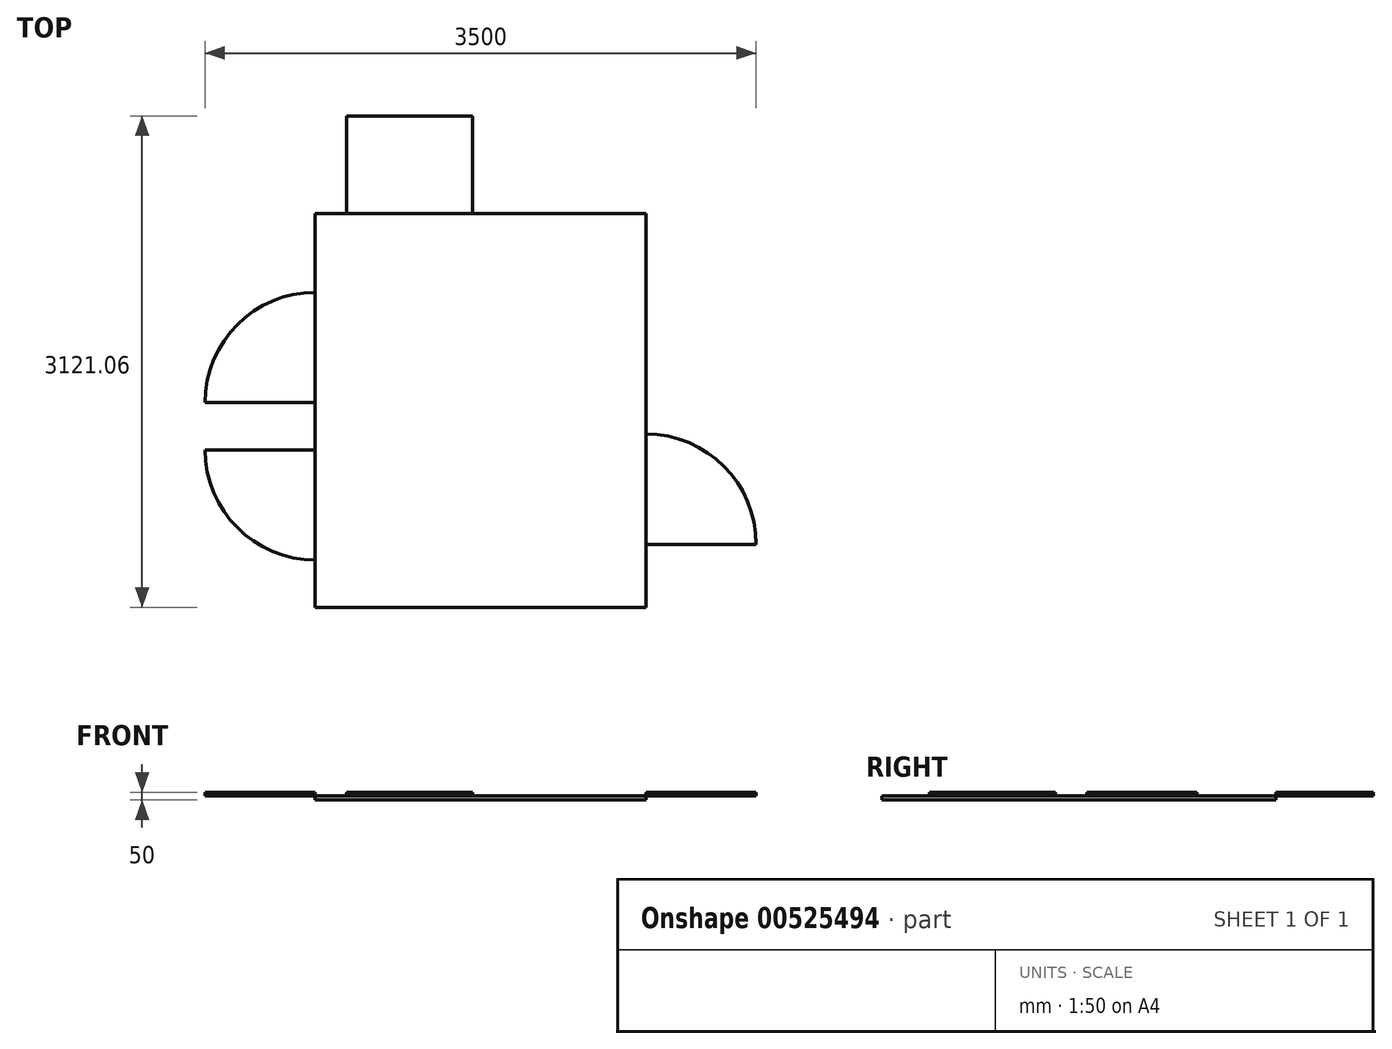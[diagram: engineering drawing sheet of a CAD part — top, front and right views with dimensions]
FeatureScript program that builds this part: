
annotation { "Feature Type Name" : "Feature", "Feature Type Description" : "" }
export const myFeature = defineFeature(function(context is Context, id is Id, definition is map)
    precondition{}
    {
        {
            var Q0;
            Q0=qCreatedBy(makeId("Top.planeOp"),FACE);
            var sketch = newSketch(context, id + "F0", { "sketchPlane" : qUnion([Q0])});
            skLineSegment(sketch, "E0.bottom", {"start": v(2100, -2500) * mm, "end": v(0, -2500) * mm});
            skLineSegment(sketch, "E0.top", {"start": v(2100, 0) * mm, "end": v(0, 0) * mm});
            skLineSegment(sketch, "E0.left", {"start": v(2100, -2500) * mm, "end": v(2100, 0) * mm});
            skLineSegment(sketch, "E0.right", {"start": v(0, -2500) * mm, "end": v(0, 0) * mm});
            skLineSegment(sketch, "E1", {"start": v(1000, 0) * mm, "end": v(1000, 621.06) * mm});
            skLineSegment(sketch, "E2", {"start": v(200, 0) * mm, "end": v(200, 621.06) * mm});
            skLineSegment(sketch, "E3", {"start": v(2100, -2100) * mm, "end": v(2800, -2100) * mm});
            skArc(sketch, "E4", {"start": v(2800, -2100) * mm, "mid": v(2594.97, -1605.03) * mm, "end": v(2100, -1400) * mm});
            skLineSegment(sketch, "E5", {"start": v(0, -1500) * mm, "end": v(-700, -1500) * mm});
            skLineSegment(sketch, "E6", {"start": v(0, -1200) * mm, "end": v(-700, -1200) * mm});
            skArc(sketch, "E7", {"start": v(-700, -1200) * mm, "mid": v(-494.97, -705.03) * mm, "end": v(0, -500) * mm});
            skArc(sketch, "E8", {"start": v(-700, -1500) * mm, "mid": v(-494.97, -1994.97) * mm, "end": v(0, -2200) * mm});
            skLineSegment(sketch, "E9", {"start": v(100, -2500) * mm, "end": v(100, -2050) * mm});
            skLineSegment(sketch, "E10", {"start": v(1000, -2500) * mm, "end": v(1000, -2050) * mm});
            skLineSegment(sketch, "E11", {"start": v(1100, -2500) * mm, "end": v(1100, -2050) * mm});
            skLineSegment(sketch, "E12", {"start": v(2000, -2500) * mm, "end": v(2000, -2050) * mm});
            skArc(sketch, "E13", {"start": v(100, -2050) * mm, "mid": v(418.2, -2181.8) * mm, "end": v(550, -2500) * mm});
            skArc(sketch, "E14", {"start": v(1000, -2050) * mm, "mid": v(681.8, -2181.8) * mm, "end": v(550, -2500) * mm});
            skArc(sketch, "E15", {"start": v(1100, -2050) * mm, "mid": v(1418.2, -2181.8) * mm, "end": v(1550, -2500) * mm});
            skArc(sketch, "E16", {"start": v(2000, -2050) * mm, "mid": v(1681.8, -2181.8) * mm, "end": v(1550, -2500) * mm});
            skLineSegment(sketch, "E17", {"start": v(200, 621.06) * mm, "end": v(1000, 621.06) * mm});
            skSolve(sketch);
        }
        {
            var Q0;
            {var subQ16=sQuery(id+"F0.wireOp",EDGE,"E9");Q0=makeQuery(id+"F0.imprint","IMPRINT",FACE,{"disambiguationData":[TD([[makeQuery(id+"F0.imprint","IMPRINT",EDGE,{"derivedFrom":subQ16}),1.0]])]});}
            var Q1;
            {var subQ0=sQuery(id+"F0.wireOp",EDGE,"E9");Q1=makeQuery(id+"F0.imprint","IMPRINT",FACE,{"disambiguationData":[TD([[makeQuery(id+"F0.imprint","IMPRINT",EDGE,{"derivedFrom":subQ0}),-1.0]])]});}
            var Q2;
            {var subQ0=sQuery(id+"F0.wireOp",EDGE,"E10");Q2=makeQuery(id+"F0.imprint","IMPRINT",FACE,{"disambiguationData":[TD([[makeQuery(id+"F0.imprint","IMPRINT",EDGE,{"derivedFrom":subQ0}),1.0]])]});}
            var Q3;
            {var subQ0=sQuery(id+"F0.wireOp",EDGE,"E11");Q3=makeQuery(id+"F0.imprint","IMPRINT",FACE,{"disambiguationData":[TD([[makeQuery(id+"F0.imprint","IMPRINT",EDGE,{"derivedFrom":subQ0}),-1.0]])]});}
            var Q4;
            {var subQ0=sQuery(id+"F0.wireOp",EDGE,"E12");Q4=makeQuery(id+"F0.imprint","IMPRINT",FACE,{"disambiguationData":[TD([[makeQuery(id+"F0.imprint","IMPRINT",EDGE,{"derivedFrom":subQ0}),1.0]])]});}
            extrude(context, id + "F1", {"entities" : qUnion([Q0, Q1, Q2, Q3, Q4]), "depth" : 25 * mm, "offsetDistance" : 25 * mm});
        }
        {
            var Q0;
            Q0=makeQuery(id+"F1.opExtrude","CAP_FACE",FACE,{"disambiguationData":[OSD([sQuery(id+"F0.wireOp",EDGE,"E0.bottom"),sQuery(id+"F0.wireOp",EDGE,"E0.top"),sQuery(id+"F0.wireOp",EDGE,"E0.left"),sQuery(id+"F0.wireOp",EDGE,"E0.right")])],"isStart":false});
            var sketch = newSketch(context, id + "F2", { "sketchPlane" : qUnion([Q0])});
            skLineSegment(sketch, "E18.0.0", {"start": v(200, 0) * mm, "end": v(1000, 0) * mm});
            skLineSegment(sketch, "E18.0.1", {"start": v(1000, 0) * mm, "end": v(1000, 621.06) * mm});
            skLineSegment(sketch, "E18.0.2", {"start": v(1000, 621.06) * mm, "end": v(200, 621.06) * mm});
            skLineSegment(sketch, "E18.0.3", {"start": v(200, 621.06) * mm, "end": v(200, 0) * mm});
            skLineSegment(sketch, "E19.0.0", {"start": v(-700, -1200) * mm, "end": v(0, -1200) * mm});
            skLineSegment(sketch, "E19.0.1", {"start": v(0, -1200) * mm, "end": v(0, -500) * mm});
            skArc(sketch, "E19.0.2", {"start": v(0, -500) * mm, "mid": v(-494.97, -705.03) * mm, "end": v(-700, -1200) * mm});
            skArc(sketch, "E20.0.0", {"start": v(-700, -1500) * mm, "mid": v(-494.97, -1994.97) * mm, "end": v(0, -2200) * mm});
            skLineSegment(sketch, "E20.0.1", {"start": v(0, -2200) * mm, "end": v(0, -1500) * mm});
            skLineSegment(sketch, "E20.0.2", {"start": v(0, -1500) * mm, "end": v(-700, -1500) * mm});
            skLineSegment(sketch, "E21.0.0", {"start": v(2100, -1400) * mm, "end": v(2100, -2100) * mm});
            skLineSegment(sketch, "E21.0.1", {"start": v(2100, -2100) * mm, "end": v(2800, -2100) * mm});
            skArc(sketch, "E21.0.2", {"start": v(2800, -2100) * mm, "mid": v(2594.97, -1605.03) * mm, "end": v(2100, -1400) * mm});
            skLineSegment(sketch, "E22.0.0", {"start": v(0, -500) * mm, "end": v(0, -2200) * mm});
            skLineSegment(sketch, "E22.0.2", {"start": v(2100, -2100) * mm, "end": v(2100, -1400) * mm});
            skLineSegment(sketch, "E22.0.3", {"start": v(1000, 0) * mm, "end": v(200, 0) * mm});
            skLineSegment(sketch, "E23.0.0", {"start": v(0, -500) * mm, "end": v(0, -1200) * mm});
            skLineSegment(sketch, "E24.0", {"start": v(1100, -2500) * mm, "end": v(1100, -2050) * mm});
            skArc(sketch, "E25.0", {"start": v(1100, -2050) * mm, "mid": v(1418.2, -2181.8) * mm, "end": v(1550, -2500) * mm});
            skArc(sketch, "E26.0", {"start": v(2000, -2050) * mm, "mid": v(1681.8, -2181.8) * mm, "end": v(1550, -2500) * mm});
            skLineSegment(sketch, "E27.0", {"start": v(2000, -2500) * mm, "end": v(2000, -2050) * mm});
            skLineSegment(sketch, "E28.0", {"start": v(1000, -2500) * mm, "end": v(1000, -2050) * mm});
            skArc(sketch, "E29.0", {"start": v(1000, -2050) * mm, "mid": v(681.8, -2181.8) * mm, "end": v(550, -2500) * mm});
            skArc(sketch, "E30.0", {"start": v(100, -2050) * mm, "mid": v(418.2, -2181.8) * mm, "end": v(550, -2500) * mm});
            skLineSegment(sketch, "E31.0", {"start": v(100, -2500) * mm, "end": v(100, -2050) * mm});
            skPoint(sketch, "E32.orphan", {"position": v(2100, -2500) * mm});
            skPoint(sketch, "E33.orphan", {"position": v(0, -2500) * mm});
            skLineSegment(sketch, "E34.trimOffspring", {"start": v(0, -1500) * mm, "end": v(0, -2200) * mm});
            skPoint(sketch, "E35.orphan", {"position": v(0, 0) * mm});
            skPoint(sketch, "E36.orphan", {"position": v(2100, 0) * mm});
            skLineSegment(sketch, "E37", {"start": v(100, -2500) * mm, "end": v(550, -2500) * mm});
            skLineSegment(sketch, "E38", {"start": v(550, -2500) * mm, "end": v(1000, -2500) * mm});
            skLineSegment(sketch, "E39", {"start": v(1100, -2500) * mm, "end": v(1550, -2500) * mm});
            skLineSegment(sketch, "E40", {"start": v(1550, -2500) * mm, "end": v(2000, -2500) * mm});
            skSolve(sketch);
        }
        {
            var Q0;
            {var subQ0=sQuery(id+"F2.wireOp",EDGE,"E20.0.0");Q0=makeQuery(id+"F2.imprint","IMPRINT",FACE,{"disambiguationData":[TD([[makeQuery(id+"F2.imprint","IMPRINT",EDGE,{"derivedFrom":subQ0}),1.0]])]});}
            var Q1;
            {var subQ0=sQuery(id+"F2.wireOp",EDGE,"E19.0.0");Q1=makeQuery(id+"F2.imprint","IMPRINT",FACE,{"disambiguationData":[TD([[makeQuery(id+"F2.imprint","IMPRINT",EDGE,{"derivedFrom":subQ0}),1.0]])]});}
            var Q2;
            {var subQ0=sQuery(id+"F2.wireOp",EDGE,"E18.0.1");Q2=makeQuery(id+"F2.imprint","IMPRINT",FACE,{"disambiguationData":[TD([[makeQuery(id+"F2.imprint","IMPRINT",EDGE,{"derivedFrom":subQ0}),1.0]])]});}
            var Q3;
            {var subQ0=sQuery(id+"F2.wireOp",EDGE,"E21.0.1");Q3=makeQuery(id+"F2.imprint","IMPRINT",FACE,{"disambiguationData":[TD([[makeQuery(id+"F2.imprint","IMPRINT",EDGE,{"derivedFrom":subQ0}),1.0]])]});}
            extrude(context, id + "F3", {"entities" : qUnion([Q0, Q1, Q2, Q3]), "operationType" : NewBodyOperationType.ADD, "depth" : 25 * mm, "offsetDistance" : 25 * mm});
        }
    });
